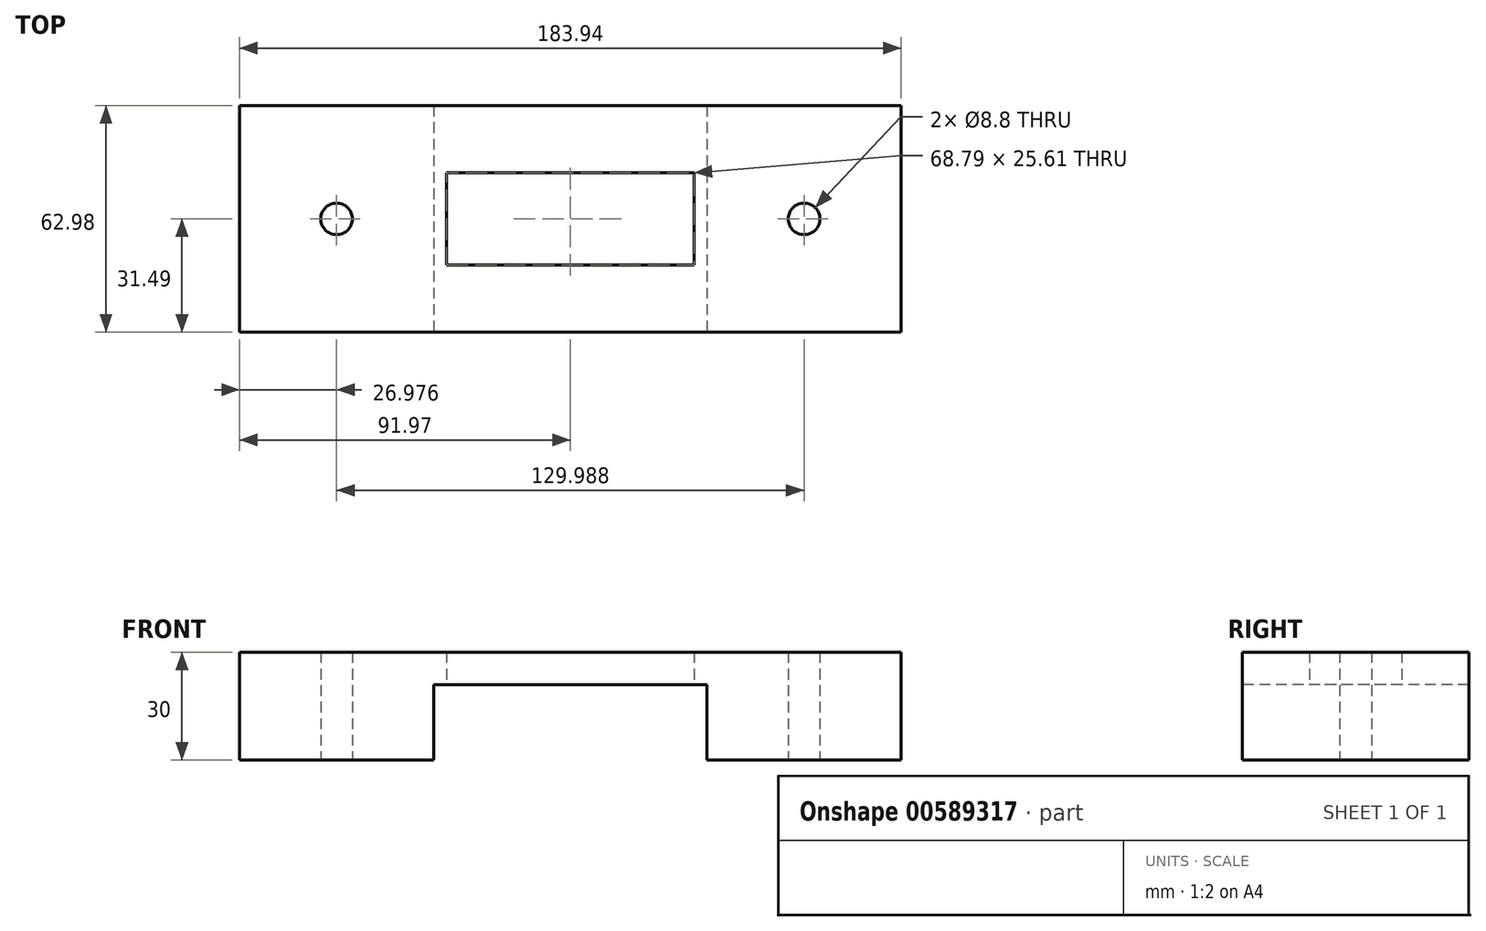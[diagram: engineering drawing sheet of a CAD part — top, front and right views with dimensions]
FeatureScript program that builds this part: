
annotation { "Feature Type Name" : "Feature", "Feature Type Description" : "" }
export const myFeature = defineFeature(function(context is Context, id is Id, definition is map)
    precondition{}
    {
        {
            var Q0;
            Q0=qCreatedBy(makeId("Top.planeOp"),FACE);
            var sketch = newSketch(context, id + "F0", { "sketchPlane" : qUnion([Q0])});
            skLineSegment(sketch, "E0.bottom", {"start": v(81.97, 31.49) * mm, "end": v(-81.97, 31.49) * mm});
            skLineSegment(sketch, "E0.top", {"start": v(81.97, -31.49) * mm, "end": v(-81.97, -31.49) * mm});
            skLineSegment(sketch, "E0.left", {"start": v(81.97, 31.49) * mm, "end": v(81.97, -31.49) * mm});
            skLineSegment(sketch, "E0.right", {"start": v(-81.97, 31.49) * mm, "end": v(-81.97, -31.49) * mm});
            skPoint(sketch, "E0.middle", {"position": v(0, 0) * mm});
            skSolve(sketch);
        }
        {
            var Q0;
            Q0 = qSketchRegion(id + "F0", true);
            extrude(context, id + "F1", {"entities" : qUnion([Q0]), "depth" : 10 * mm, "offsetDistance" : 25.4 * mm});
        }
        {
            var Q0;
            Q0=makeQuery(id+"F1.opExtrude","CAP_FACE",FACE,{"disambiguationData":[OSD([sQuery(id+"F0.wireOp",EDGE,"E0.bottom"),sQuery(id+"F0.wireOp",EDGE,"E0.top"),sQuery(id+"F0.wireOp",EDGE,"E0.left"),sQuery(id+"F0.wireOp",EDGE,"E0.right")])],"isStart":false});
            extrude(context, id + "F2", {"entities" : qUnion([Q0]), "operationType" : NewBodyOperationType.ADD, "depth" : 20 * mm, "offsetDistance" : 25.4 * mm});
        }
        {
            var Q0;
            Q0=qCreatedBy(makeId("Front.planeOp"),FACE);
            var sketch = newSketch(context, id + "F3", { "sketchPlane" : qUnion([Q0])});
            skLineSegment(sketch, "E1.bottom", {"start": v(38.02, 20.98) * mm, "end": v(-38.02, 20.98) * mm});
            skLineSegment(sketch, "E1.top", {"start": v(38.02, -20.98) * mm, "end": v(-38.02, -20.98) * mm});
            skLineSegment(sketch, "E1.left", {"start": v(38.02, 20.98) * mm, "end": v(38.02, -20.98) * mm});
            skLineSegment(sketch, "E1.right", {"start": v(-38.02, 20.98) * mm, "end": v(-38.02, -20.98) * mm});
            skPoint(sketch, "E1.middle", {"position": v(0, 0) * mm});
            skSolve(sketch);
        }
        {
            var Q0;
            Q0 = qSketchRegion(id + "F3", true);
            extrude(context, id + "F4", {"entities" : qUnion([Q0]), "operationType" : NewBodyOperationType.REMOVE, "endBound" : BoundingType.SYMMETRIC, "oppositeDirection" : true, "depth" : 100 * mm, "offsetDistance" : 25.4 * mm});
        }
        {
            var Q0;
            Q0=makeQuery(id+"F2.opExtrude","CAP_FACE",FACE,{"disambiguationData":[OSD([sQuery(id+"F0.wireOp",EDGE,"E0.bottom"),sQuery(id+"F0.wireOp",EDGE,"E0.top"),sQuery(id+"F0.wireOp",EDGE,"E0.left"),sQuery(id+"F0.wireOp",EDGE,"E0.right")])],"isStart":false});
            extrude(context, id + "F5", {"entities" : qUnion([Q0]), "operationType" : NewBodyOperationType.ADD, "depth" : 10 * mm, "offsetDistance" : 25.4 * mm});
        }
        {
            var Q0;
            {var subQ0=sQuery(id+"F0.wireOp",EDGE,"E0.left");Q0=makeQuery(id+"F5.boolean.opBoolean","MERGE",FACE,{"derivedFrom":[makeQuery(id+"F2.boolean.opBoolean","MERGE",FACE,{"derivedFrom":[makeQuery(id+"F1.opExtrude","SWEPT_FACE",FACE,{"disambiguationData":[OSD([subQ0])]}),makeQuery(id+"F2.opExtrude","SWEPT_FACE",FACE,{"disambiguationData":[OSD([subQ0])]})]}),makeQuery(id+"F5.opExtrude","SWEPT_FACE",FACE,{"disambiguationData":[OSD([subQ0])]})]});}
            extrude(context, id + "F6", {"entities" : qUnion([Q0]), "operationType" : NewBodyOperationType.ADD, "depth" : 10 * mm, "offsetDistance" : 25.4 * mm});
        }
        {
            var Q0;
            {var subQ0=sQuery(id+"F0.wireOp",EDGE,"E0.right");Q0=makeQuery(id+"F5.boolean.opBoolean","MERGE",FACE,{"derivedFrom":[makeQuery(id+"F2.boolean.opBoolean","MERGE",FACE,{"derivedFrom":[makeQuery(id+"F1.opExtrude","SWEPT_FACE",FACE,{"disambiguationData":[OSD([subQ0])]}),makeQuery(id+"F2.opExtrude","SWEPT_FACE",FACE,{"disambiguationData":[OSD([subQ0])]})]}),makeQuery(id+"F5.opExtrude","SWEPT_FACE",FACE,{"disambiguationData":[OSD([subQ0])]})]});}
            extrude(context, id + "F7", {"entities" : qUnion([Q0]), "operationType" : NewBodyOperationType.ADD, "depth" : 10 * mm, "offsetDistance" : 25.4 * mm});
        }
        {
            var Q0;
            {var subQ0=sQuery(id+"F0.wireOp",EDGE,"E0.right");var subQ1=sQuery(id+"F0.wireOp",EDGE,"E0.bottom");var subQ2=sQuery(id+"F0.wireOp",EDGE,"E0.top");Q0=makeQuery(id+"F7.boolean.opBoolean","MERGE",FACE,{"derivedFrom":[makeQuery(id+"F4.boolean.opBoolean","SPLIT",FACE,{"disambiguationData":[TD([makeQuery(id+"F1.opExtrude","SWEPT_FACE",FACE,{"disambiguationData":[OSD([subQ0])]})])],"derivedFrom":makeQuery(id+"F1.opExtrude","CAP_FACE",FACE,{"disambiguationData":[OSD([subQ1,subQ2,sQuery(id+"F0.wireOp",EDGE,"E0.left"),subQ0])],"isStart":true})}),makeQuery(id+"F7.opExtrude","SWEPT_FACE",FACE,{"disambiguationData":[OSD([subQ0]),TDD([makeQuery(id+"F1.opExtrude","CAP_EDGE",EDGE,{"disambiguationData":[OSD([subQ0])],"isStart":true})])]})]});}
            var sketch = newSketch(context, id + "F8", { "sketchPlane" : qUnion([Q0])});
            skLineSegment(sketch, "E2", {"start": v(-38.02, 0) * mm, "end": v(-91.97, 0) * mm});
            skLineSegment(sketch, "E3", {"start": v(-65, 0) * mm, "end": v(-65, 31.49) * mm});
            skLineSegment(sketch, "E4", {"start": v(-65, 31.49) * mm, "end": v(-65, -31.49) * mm});
            skSolve(sketch);
        }
        {
            var Q0;
            Q0=sQuery(id+"F8.wireOp",VERTEX,"E3.start");
            var Q1;
            Q1=makeQuery(id+"F1.opExtrude","SWEPT_BODY",BODY,{"disambiguationData":[OSD([sQuery(id+"F0.wireOp",EDGE,"E0.bottom"),sQuery(id+"F0.wireOp",EDGE,"E0.top"),sQuery(id+"F0.wireOp",EDGE,"E0.left"),sQuery(id+"F0.wireOp",EDGE,"E0.right")])]});
            hole(context, id + "F9", {"style" : HoleStyle.SIMPLE, "endStyle" : HoleEndStyle.THROUGH, "standardTappedOrClearance" : lookupTablePath({ "standard" : "ISO", "fit" : "Normal", "size" : "M8", "type" : "Clearance" }), "standardBlindInLast" : lookupTablePath({ "fit" : "Standard", "standard" : "ISO", "size" : "M8", "type" : "Clearance" }), "holeDiameter" : 8.8 * mm, "majorDiameter" : 5 * mm, "isTappedThrough" : true, "tappedDepth" : 12.7 * mm, "tapClearance" : 3, "locations" : qUnion([Q0]), "scope" : qUnion([Q1])});
        }
        {
            var Q0;
            {var subQ0=sQuery(id+"F0.wireOp",EDGE,"E0.left");var subQ1=sQuery(id+"F0.wireOp",EDGE,"E0.bottom");var subQ2=sQuery(id+"F0.wireOp",EDGE,"E0.top");Q0=makeQuery(id+"F6.boolean.opBoolean","MERGE",FACE,{"derivedFrom":[makeQuery(id+"F4.boolean.opBoolean","SPLIT",FACE,{"disambiguationData":[TD([makeQuery(id+"F1.opExtrude","SWEPT_FACE",FACE,{"disambiguationData":[OSD([subQ0])]})])],"derivedFrom":makeQuery(id+"F1.opExtrude","CAP_FACE",FACE,{"disambiguationData":[OSD([subQ1,subQ2,subQ0,sQuery(id+"F0.wireOp",EDGE,"E0.right")])],"isStart":true})}),makeQuery(id+"F6.opExtrude","SWEPT_FACE",FACE,{"disambiguationData":[OSD([subQ0]),TDD([makeQuery(id+"F1.opExtrude","CAP_EDGE",EDGE,{"disambiguationData":[OSD([subQ0])],"isStart":true})])]})]});}
            var sketch = newSketch(context, id + "F10", { "sketchPlane" : qUnion([Q0])});
            skLineSegment(sketch, "E5", {"start": v(38.02, 0) * mm, "end": v(91.97, 0) * mm});
            skLineSegment(sketch, "E6", {"start": v(91.97, 0) * mm, "end": v(65, 0) * mm});
            skLineSegment(sketch, "E7", {"start": v(65, 0) * mm, "end": v(65, 31.49) * mm});
            skLineSegment(sketch, "E8", {"start": v(65, 31.49) * mm, "end": v(65, -31.49) * mm});
            skSolve(sketch);
        }
        {
            var Q0;
            Q0=sQuery(id+"F10.wireOp",VERTEX,"E7.start");
            var Q1;
            Q1=makeQuery(id+"F1.opExtrude","SWEPT_BODY",BODY,{"disambiguationData":[OSD([sQuery(id+"F0.wireOp",EDGE,"E0.bottom"),sQuery(id+"F0.wireOp",EDGE,"E0.top"),sQuery(id+"F0.wireOp",EDGE,"E0.left"),sQuery(id+"F0.wireOp",EDGE,"E0.right")])]});
            hole(context, id + "F11", {"style" : HoleStyle.SIMPLE, "endStyle" : HoleEndStyle.THROUGH, "standardTappedOrClearance" : lookupTablePath({ "standard" : "ISO", "fit" : "Normal", "size" : "M8", "type" : "Clearance" }), "standardBlindInLast" : lookupTablePath({ "fit" : "Standard", "standard" : "ISO", "size" : "M8", "type" : "Clearance" }), "holeDiameter" : 8.8 * mm, "majorDiameter" : 6.35 * mm, "isTappedThrough" : true, "tappedDepth" : 12.7 * mm, "tapClearance" : 3, "locations" : qUnion([Q0]), "scope" : qUnion([Q1])});
        }
        {
            var Q0;
            Q0=makeQuery(id+"F4.boolean.opBoolean","COPY",FACE,{"derivedFrom":makeQuery(id+"F4.opExtrude","SWEPT_FACE",FACE,{"disambiguationData":[OSD([sQuery(id+"F3.wireOp",EDGE,"E1.bottom")])]})});
            var sketch = newSketch(context, id + "F12", { "sketchPlane" : qUnion([Q0])});
            skLineSegment(sketch, "E9.bottom", {"start": v(34.4, 12.8) * mm, "end": v(-34.4, 12.8) * mm});
            skLineSegment(sketch, "E9.top", {"start": v(34.4, -12.8) * mm, "end": v(-34.4, -12.8) * mm});
            skLineSegment(sketch, "E9.left", {"start": v(34.4, 12.8) * mm, "end": v(34.4, -12.8) * mm});
            skLineSegment(sketch, "E9.right", {"start": v(-34.4, 12.8) * mm, "end": v(-34.4, -12.8) * mm});
            skPoint(sketch, "E9.middle", {"position": v(0, 0) * mm});
            skSolve(sketch);
        }
        {
            var Q0;
            Q0=makeQuery(id+"F12.imprint","IMPRINT",FACE,{"disambiguationData":[TD([[makeQuery(id+"F12.imprint","IMPRINT",EDGE,{"derivedFrom":sQuery(id+"F12.wireOp",EDGE,"E9.bottom")}),1.0]])]});
            extrude(context, id + "F13", {"entities" : qUnion([Q0]), "operationType" : NewBodyOperationType.REMOVE, "endBound" : BoundingType.SYMMETRIC, "oppositeDirection" : true, "depth" : 50 * mm, "offsetDistance" : 25.4 * mm});
        }
        {
            var Q0;
            {var subQ0=sQuery(id+"F0.wireOp",EDGE,"E0.right");var subQ1=sQuery(id+"F0.wireOp",EDGE,"E0.bottom");var subQ2=sQuery(id+"F0.wireOp",EDGE,"E0.top");Q0=makeQuery(id+"F7.boolean.opBoolean","MERGE",FACE,{"derivedFrom":[makeQuery(id+"F4.boolean.opBoolean","SPLIT",FACE,{"disambiguationData":[TD([makeQuery(id+"F1.opExtrude","SWEPT_FACE",FACE,{"disambiguationData":[OSD([subQ0])]})])],"derivedFrom":makeQuery(id+"F1.opExtrude","CAP_FACE",FACE,{"disambiguationData":[OSD([subQ1,subQ2,sQuery(id+"F0.wireOp",EDGE,"E0.left"),subQ0])],"isStart":true})}),makeQuery(id+"F7.opExtrude","SWEPT_FACE",FACE,{"disambiguationData":[OSD([subQ0]),TDD([makeQuery(id+"F1.opExtrude","CAP_EDGE",EDGE,{"disambiguationData":[OSD([subQ0])],"isStart":true})])]})]});}
            extrude(context, id + "F14", {"entities" : qUnion([Q0]), "operationType" : NewBodyOperationType.REMOVE, "oppositeDirection" : true, "depth" : 10 * mm, "offsetDistance" : 25.4 * mm});
        }
        {
            var Q0;
            {var subQ0=sQuery(id+"F0.wireOp",EDGE,"E0.left");var subQ1=sQuery(id+"F0.wireOp",EDGE,"E0.bottom");var subQ2=sQuery(id+"F0.wireOp",EDGE,"E0.top");Q0=makeQuery(id+"F6.boolean.opBoolean","MERGE",FACE,{"derivedFrom":[makeQuery(id+"F4.boolean.opBoolean","SPLIT",FACE,{"disambiguationData":[TD([makeQuery(id+"F1.opExtrude","SWEPT_FACE",FACE,{"disambiguationData":[OSD([subQ0])]})])],"derivedFrom":makeQuery(id+"F1.opExtrude","CAP_FACE",FACE,{"disambiguationData":[OSD([subQ1,subQ2,subQ0,sQuery(id+"F0.wireOp",EDGE,"E0.right")])],"isStart":true})}),makeQuery(id+"F6.opExtrude","SWEPT_FACE",FACE,{"disambiguationData":[OSD([subQ0]),TDD([makeQuery(id+"F1.opExtrude","CAP_EDGE",EDGE,{"disambiguationData":[OSD([subQ0])],"isStart":true})])]})]});}
            extrude(context, id + "F15", {"entities" : qUnion([Q0]), "operationType" : NewBodyOperationType.REMOVE, "oppositeDirection" : true, "depth" : 10 * mm, "offsetDistance" : 25.4 * mm});
        }
        {
            var Q0;
            Q0=makeQuery(id+"F15.boolean.opBoolean","COPY",FACE,{"derivedFrom":makeQuery(id+"F15.opExtrude","CAP_FACE",FACE,{"disambiguationData":[OSD([sQuery(id+"F0.wireOp",EDGE,"E0.bottom"),sQuery(id+"F0.wireOp",EDGE,"E0.top"),sQuery(id+"F0.wireOp",EDGE,"E0.left"),sQuery(id+"F0.wireOp",EDGE,"E0.right")])],"isStart":false})});
            extrude(context, id + "F16", {"entities" : qUnion([Q0]), "operationType" : NewBodyOperationType.REMOVE, "oppositeDirection" : true, "depth" : 5 * mm, "offsetDistance" : 25.4 * mm});
        }
        {
            var Q0;
            Q0=makeQuery(id+"F14.boolean.opBoolean","COPY",FACE,{"derivedFrom":makeQuery(id+"F14.opExtrude","CAP_FACE",FACE,{"disambiguationData":[OSD([sQuery(id+"F0.wireOp",EDGE,"E0.bottom"),sQuery(id+"F0.wireOp",EDGE,"E0.top"),sQuery(id+"F0.wireOp",EDGE,"E0.left"),sQuery(id+"F0.wireOp",EDGE,"E0.right")])],"isStart":false})});
            extrude(context, id + "F17", {"entities" : qUnion([Q0]), "operationType" : NewBodyOperationType.REMOVE, "oppositeDirection" : true, "depth" : 5 * mm, "offsetDistance" : 25.4 * mm});
        }
        {
            var Q0;
            Q0=makeQuery(id+"F4.boolean.opBoolean","COPY",FACE,{"derivedFrom":makeQuery(id+"F4.opExtrude","SWEPT_FACE",FACE,{"disambiguationData":[OSD([sQuery(id+"F3.wireOp",EDGE,"E1.bottom")])]})});
            extrude(context, id + "F18", {"entities" : qUnion([Q0]), "operationType" : NewBodyOperationType.REMOVE, "oppositeDirection" : true, "depth" : 15 * mm, "offsetDistance" : 25.4 * mm});
        }
        {
            var Q0;
            {var subQ0=sQuery(id+"F0.wireOp",EDGE,"E0.right");var subQ1=sQuery(id+"F0.wireOp",EDGE,"E0.left");Q0=makeQuery(id+"F7.boolean.opBoolean","MERGE",FACE,{"derivedFrom":[makeQuery(id+"F6.boolean.opBoolean","MERGE",FACE,{"derivedFrom":[makeQuery(id+"F5.opExtrude","CAP_FACE",FACE,{"disambiguationData":[OSD([sQuery(id+"F0.wireOp",EDGE,"E0.bottom"),sQuery(id+"F0.wireOp",EDGE,"E0.top"),subQ1,subQ0])],"isStart":false}),makeQuery(id+"F6.opExtrude","SWEPT_FACE",FACE,{"disambiguationData":[OSD([subQ1]),TDD([makeQuery(id+"F5.opExtrude","CAP_EDGE",EDGE,{"disambiguationData":[OSD([subQ1])],"isStart":false})])]})]}),makeQuery(id+"F7.opExtrude","SWEPT_FACE",FACE,{"disambiguationData":[OSD([subQ0]),TDD([makeQuery(id+"F5.opExtrude","CAP_EDGE",EDGE,{"disambiguationData":[OSD([subQ0])],"isStart":false})])]})]});}
            extrude(context, id + "F19", {"entities" : qUnion([Q0]), "operationType" : NewBodyOperationType.ADD, "depth" : 5 * mm, "offsetDistance" : 25.4 * mm});
        }
    });
